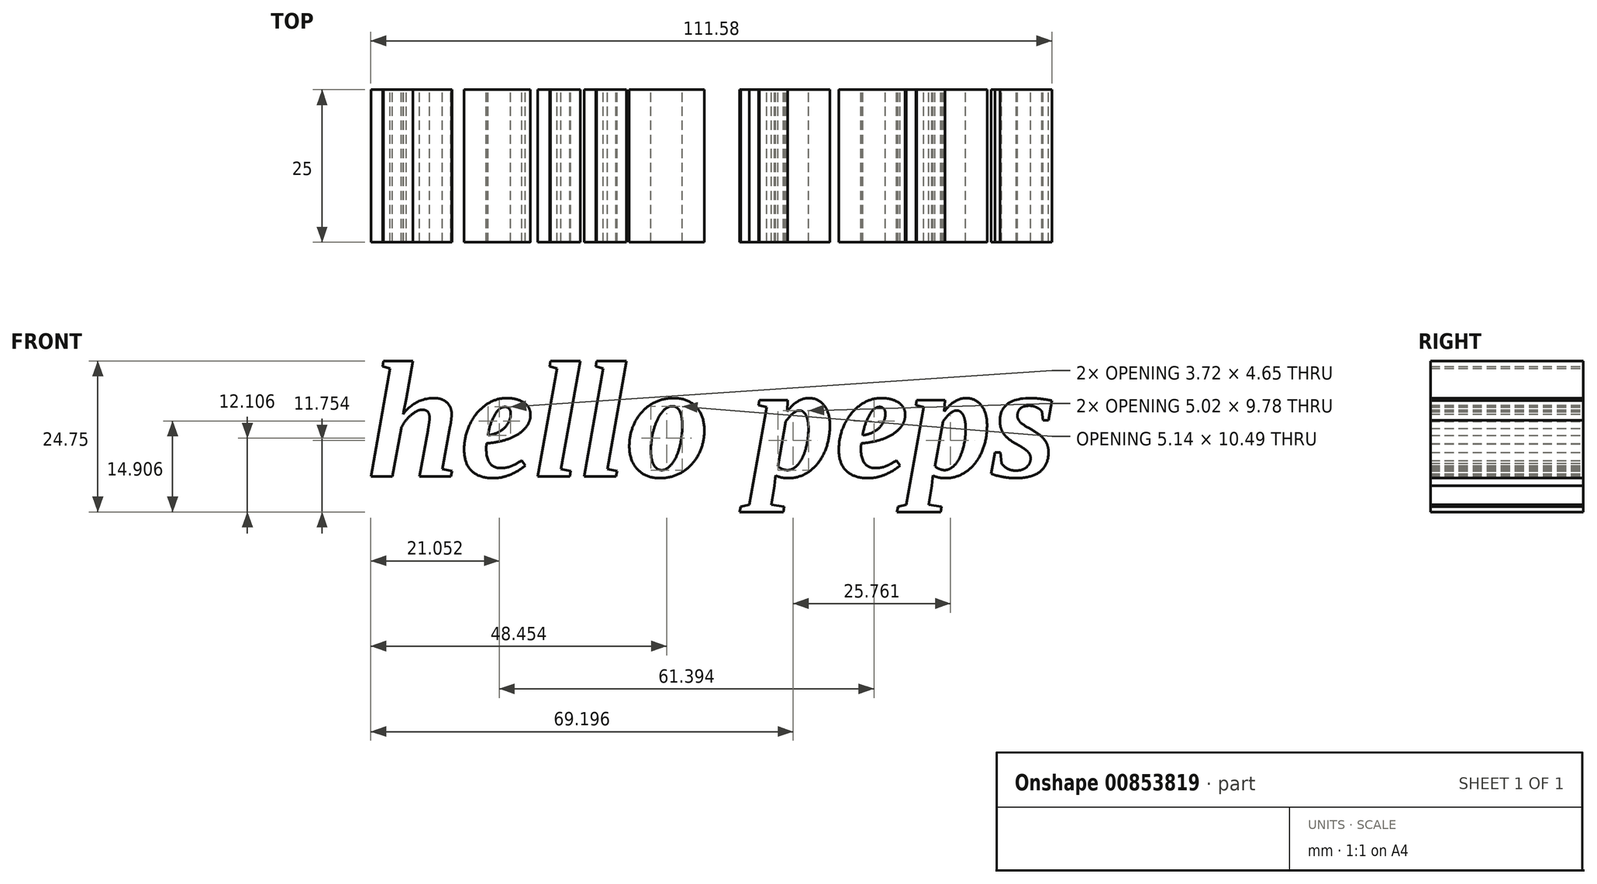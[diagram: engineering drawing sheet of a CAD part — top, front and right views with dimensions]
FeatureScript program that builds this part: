
annotation { "Feature Type Name" : "Feature", "Feature Type Description" : "" }
export const myFeature = defineFeature(function(context is Context, id is Id, definition is map)
    precondition{}
    {
        {
            var Q0;
            Q0=qCreatedBy(makeId("Front.planeOp"),FACE);
            var sketch = newSketch(context, id + "F0", { "sketchPlane" : qUnion([Q0])});
            skText(sketch, "E0", { "text": "hello peps", "fontName": "Tinos-BoldItalic.ttf"});
            const initialGuessF0  = {"E0": [-0.02767, 0.019, 1, 0, 0.01965]};
            skSetInitialGuess(sketch, initialGuessF0);
            skSolve(sketch);
        }
        {
            var Q0;
            Q0 = qSketchRegion(id + "F0", true);
            extrude(context, id + "F1", {"entities" : qUnion([Q0]), "depth" : 25 * mm, "offsetDistance" : 25 * mm});
        }
    });
